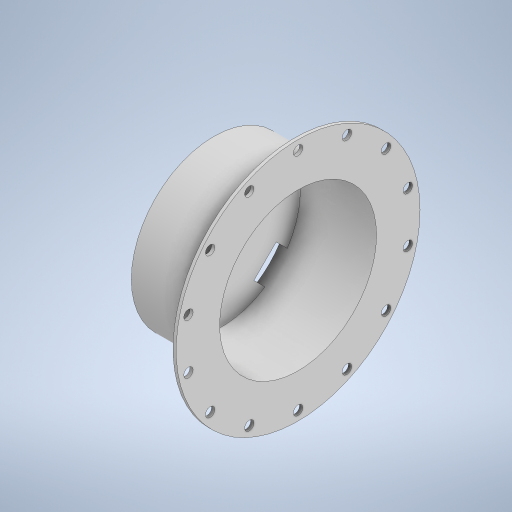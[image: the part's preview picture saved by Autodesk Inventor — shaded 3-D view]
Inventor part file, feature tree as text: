
AUTODESK INVENTOR PART (.ipt)
format: ipt  version: 2023 (Build 270158000, 158)  size: 346,112 bytes
history: native  units: mm
features: extrude x4, sketch x3
ambient origin geometry x8: Origin, YZ Plane, XZ Plane, XY Plane, X Axis, Y Axis, Z Axis, Center Point
bodies: Solid1 (feature_tree)
feature tree (7):
  extrude  "Extrusion1"  Depth=3.5mm
  extrude  "Extrusion2"  Depth=105.0mm
  extrude  "Extrusion4"  Depth=5.0mm TaperAngle=0.0deg
  extrude  "Extrusion6"  Depth=2.0mm
  sketch  "Sketch1"  dims[d0=38.0mm d1=3.5mm]
  sketch  "Sketch2"  dims[d2=40.0mm d4=360.0deg d6=105.0mm]
  sketch  "Sketch6"  dims[d7=80.0mm d8=5.0mm d9=0.0mm d10=105.0mm d11=53.5mm d12=0.0mm d27=30.0mm d28=10.0mm d29=45.0deg d30=10.0mm d31=10.0mm d32=0.0mm d34=10.0mm d35=143.0mm d36=6.0mm d37=70.0mm d39=360.0deg d41=155.0mm d44=140.0mm d46=360.0deg d48=2.0mm d49=0.0mm]
